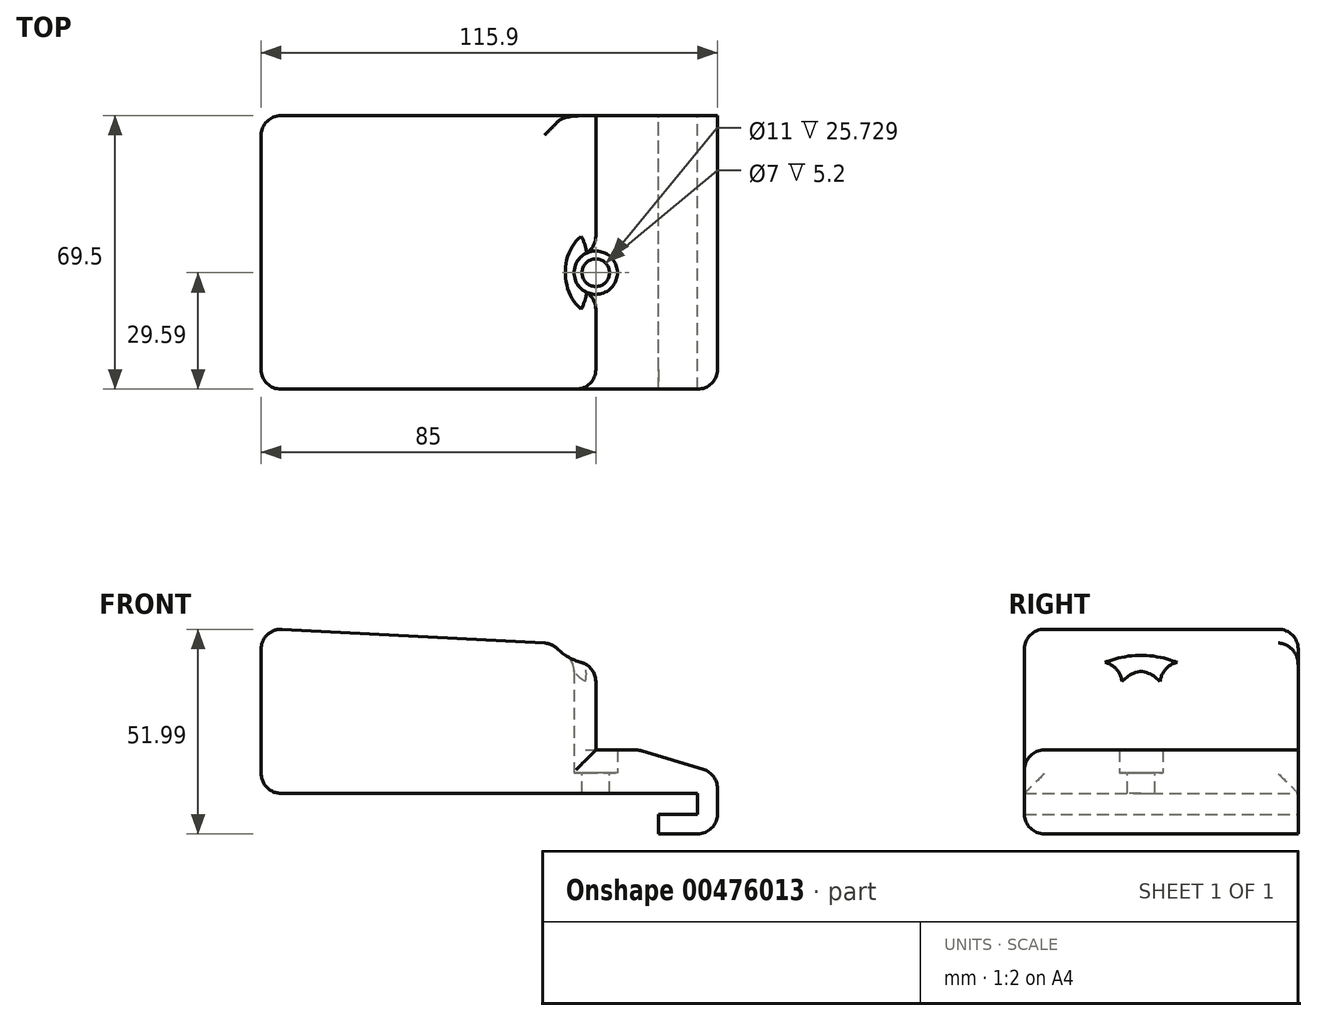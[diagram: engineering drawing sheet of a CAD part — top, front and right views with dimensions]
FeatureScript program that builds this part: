
annotation { "Feature Type Name" : "Feature", "Feature Type Description" : "" }
export const myFeature = defineFeature(function(context is Context, id is Id, definition is map)
    precondition{}
    {
        {
            var Q0;
            Q0=qCreatedBy(makeId("Front.planeOp"),FACE);
            var sketch = newSketch(context, id + "F0", { "sketchPlane" : qUnion([Q0])});
            skLineSegment(sketch, "E0", {"start": v(0, 37.5) * mm, "end": v(-85, 41.95) * mm});
            skLineSegment(sketch, "E1", {"start": v(-85, 41.95) * mm, "end": v(-85, 0) * mm});
            skLineSegment(sketch, "E2", {"start": v(0, 37.5) * mm, "end": v(0, 11) * mm});
            skLineSegment(sketch, "E3", {"start": v(0, 11) * mm, "end": v(11, 11) * mm});
            skLineSegment(sketch, "E4", {"start": v(30.9, 0) * mm, "end": v(30.9, -10.3) * mm});
            skLineSegment(sketch, "E5", {"start": v(30.9, -10.3) * mm, "end": v(15.9, -10.3) * mm});
            skLineSegment(sketch, "E6", {"start": v(15.9, -10.3) * mm, "end": v(15.9, -5.3) * mm});
            skLineSegment(sketch, "E7", {"start": v(15.9, -5.3) * mm, "end": v(25.9, -5.3) * mm});
            skLineSegment(sketch, "E8", {"start": v(25.9, -5.3) * mm, "end": v(25.9, 0) * mm});
            skLineSegment(sketch, "E9", {"start": v(25.9, 0) * mm, "end": v(-85, 0) * mm});
            skLineSegment(sketch, "E10", {"start": v(30.9, 0) * mm, "end": v(30.9, 5) * mm});
            skLineSegment(sketch, "E11", {"start": v(11, 11) * mm, "end": v(30.9, 5) * mm});
            skSolve(sketch);
        }
        {
            var Q0;
            Q0 = qSketchRegion(id + "F0", true);
            extrude(context, id + "F1", {"entities" : qUnion([Q0]), "depth" : 69.5 * mm});
        }
        {
            var Q0;
            Q0=makeQuery(id+"F1.opExtrude","CAP_FACE",FACE,{"disambiguationData":[OSD([sQuery(id+"F0.wireOp",EDGE,"E0"),sQuery(id+"F0.wireOp",EDGE,"E1"),sQuery(id+"F0.wireOp",EDGE,"Xl3YUMXG-rWPs-34HO-qeN5-JV3TIRV4gZtY"),sQuery(id+"F0.wireOp",EDGE,"MgZQELxX-fbr9-p0Fq-y226-Uqsu6zS7fgz1")])],"isStart":true});
            var sketch = newSketch(context, id + "F2", { "sketchPlane" : qUnion([Q0])});
            skCircle(sketch, "E12", {"center": v(0, 46.76) * mm, "radius": 14 * mm});
            skSolve(sketch);
        }
        {
            var Q0;
            Q0 = qSketchRegion(id + "F2", true);
            extrude(context, id + "F3", {"entities" : qUnion([Q0]), "operationType" : NewBodyOperationType.REMOVE, "endBound" : BoundingType.THROUGH_ALL, "oppositeDirection" : true, "depth" : 25 * mm});
        }
        {
            var Q0;
            Q0=makeQuery(id+"F1.opExtrude","SWEPT_FACE",FACE,{"disambiguationData":[OSD([sQuery(id+"F0.wireOp",EDGE,"E3")])]});
            var sketch = newSketch(context, id + "F4", { "sketchPlane" : qUnion([Q0])});
            skCircle(sketch, "E13", {"center": v(0, -39.91) * mm, "radius": 5.5 * mm});
            skSolve(sketch);
        }
        {
            var Q0;
            Q0 = qSketchRegion(id + "F4", true);
            extrude(context, id + "F5", {"entities" : qUnion([Q0]), "operationType" : NewBodyOperationType.REMOVE, "endBound" : BoundingType.THROUGH_ALL, "depth" : 25 * mm});
        }
        {
            var Q0;
            Q0 = qSketchRegion(id + "F4", true);
            extrude(context, id + "F6", {"entities" : qUnion([Q0]), "operationType" : NewBodyOperationType.REMOVE, "oppositeDirection" : true, "depth" : 5.8 * mm});
        }
        {
            var Q0;
            Q0=makeQuery(id+"F5.boolean.opBoolean","MERGE",FACE,{"derivedFrom":[makeQuery(id+"F1.opExtrude","SWEPT_FACE",FACE,{"disambiguationData":[OSD([sQuery(id+"F0.wireOp",EDGE,"E3")])]}),makeQuery(id+"F5.opExtrude","CAP_FACE",FACE,{"disambiguationData":[OSD([sQuery(id+"F4.wireOp",EDGE,"E13")])],"isStart":true})]});
            var sketch = newSketch(context, id + "F7", { "sketchPlane" : qUnion([Q0])});
            skCircle(sketch, "E14", {"center": v(0, -39.91) * mm, "radius": 3.5 * mm});
            skSolve(sketch);
        }
        {
            var Q0;
            Q0 = qSketchRegion(id + "F7", true);
            extrude(context, id + "F8", {"entities" : qUnion([Q0]), "operationType" : NewBodyOperationType.REMOVE, "endBound" : BoundingType.THROUGH_ALL, "oppositeDirection" : true, "depth" : 25 * mm});
        }
        {
            var Q0;
            Q0=makeQuery(id+"F1.opExtrude","SWEPT_EDGE",EDGE,{"disambiguationData":[OSD([sQuery(id+"F0.wireOp",EDGE,"E10"),sQuery(id+"F0.wireOp",EDGE,"E11")])]});
            var Q1;
            Q1=makeQuery(id+"F1.opExtrude","SWEPT_EDGE",EDGE,{"disambiguationData":[OSD([sQuery(id+"F0.wireOp",EDGE,"E3"),sQuery(id+"F0.wireOp",EDGE,"E11")])]});
            var Q2;
            Q2=makeQuery(id+"F1.opExtrude","CAP_EDGE",EDGE,{"disambiguationData":[OSD([sQuery(id+"F0.wireOp",EDGE,"E11")])],"isStart":false});
            var Q3;
            Q3=makeQuery(id+"F1.opExtrude","CAP_EDGE",EDGE,{"disambiguationData":[OSD([sQuery(id+"F0.wireOp",EDGE,"E3")])],"isStart":false});
            var Q4;
            Q4=makeQuery(id+"F1.opExtrude","CAP_EDGE",EDGE,{"disambiguationData":[OSD([sQuery(id+"F0.wireOp",EDGE,"E4"),sQuery(id+"F0.wireOp",EDGE,"E10")])],"isStart":false});
            var Q5;
            Q5=makeQuery(id+"F1.opExtrude","SWEPT_EDGE",EDGE,{"disambiguationData":[OSD([sQuery(id+"F0.wireOp",EDGE,"E4"),sQuery(id+"F0.wireOp",EDGE,"E5")])]});
            var Q6;
            Q6=makeQuery(id+"F1.opExtrude","CAP_EDGE",EDGE,{"disambiguationData":[OSD([sQuery(id+"F0.wireOp",EDGE,"E5")])],"isStart":false});
            var Q7;
            {var subQ0=sQuery(id+"F0.wireOp",EDGE,"E2");var subQ1=makeQuery(id+"F1.opExtrude","SWEPT_FACE",FACE,{"disambiguationData":[OSD([subQ0])]});var subQ2=makeQuery(id+"F3.opExtrude","SWEPT_FACE",FACE,{"disambiguationData":[OSD([sQuery(id+"F2.wireOp",EDGE,"E12")])]});Q7=makeQuery(id+"F5.boolean.opBoolean","SPLIT",EDGE,{"disambiguationData":[TD([makeQuery(id+"F1.opExtrude","CAP_FACE",FACE,{"disambiguationData":[OSD([sQuery(id+"F0.wireOp",EDGE,"E0"),sQuery(id+"F0.wireOp",EDGE,"E1"),subQ0,sQuery(id+"F0.wireOp",EDGE,"E3"),sQuery(id+"F0.wireOp",EDGE,"E4"),sQuery(id+"F0.wireOp",EDGE,"E5"),sQuery(id+"F0.wireOp",EDGE,"E6"),sQuery(id+"F0.wireOp",EDGE,"E7"),sQuery(id+"F0.wireOp",EDGE,"E8"),sQuery(id+"F0.wireOp",EDGE,"E9"),sQuery(id+"F0.wireOp",EDGE,"E10"),sQuery(id+"F0.wireOp",EDGE,"E11")])],"isStart":false})])],"derivedFrom":makeQuery(id+"F3.boolean.opBoolean","INTERSECT",EDGE,{"derivedFrom":[subQ1,subQ2]})});}
            var Q8;
            {var subQ0=sQuery(id+"F0.wireOp",EDGE,"E2");var subQ1=makeQuery(id+"F1.opExtrude","SWEPT_FACE",FACE,{"disambiguationData":[OSD([subQ0])]});var subQ2=makeQuery(id+"F3.opExtrude","SWEPT_FACE",FACE,{"disambiguationData":[OSD([sQuery(id+"F2.wireOp",EDGE,"E12")])]});Q8=makeQuery(id+"F5.boolean.opBoolean","SPLIT",EDGE,{"disambiguationData":[TD([makeQuery(id+"F1.opExtrude","CAP_FACE",FACE,{"disambiguationData":[OSD([sQuery(id+"F0.wireOp",EDGE,"E0"),sQuery(id+"F0.wireOp",EDGE,"E1"),subQ0,sQuery(id+"F0.wireOp",EDGE,"E3"),sQuery(id+"F0.wireOp",EDGE,"E4"),sQuery(id+"F0.wireOp",EDGE,"E5"),sQuery(id+"F0.wireOp",EDGE,"E6"),sQuery(id+"F0.wireOp",EDGE,"E7"),sQuery(id+"F0.wireOp",EDGE,"E8"),sQuery(id+"F0.wireOp",EDGE,"E9"),sQuery(id+"F0.wireOp",EDGE,"E10"),sQuery(id+"F0.wireOp",EDGE,"E11")])],"isStart":true})])],"derivedFrom":makeQuery(id+"F3.boolean.opBoolean","INTERSECT",EDGE,{"derivedFrom":[subQ1,subQ2]})});}
            var Q9;
            Q9=makeQuery(id+"F3.boolean.opBoolean","INTERSECT",EDGE,{"derivedFrom":[makeQuery(id+"F1.opExtrude","SWEPT_FACE",FACE,{"disambiguationData":[OSD([sQuery(id+"F0.wireOp",EDGE,"E0")])]}),makeQuery(id+"F3.opExtrude","SWEPT_FACE",FACE,{"disambiguationData":[OSD([sQuery(id+"F2.wireOp",EDGE,"E12")])]})]});
            var Q10;
            Q10=makeQuery(id+"F1.opExtrude","CAP_EDGE",EDGE,{"disambiguationData":[OSD([sQuery(id+"F0.wireOp",EDGE,"E2")])],"isStart":false});
            var Q11;
            Q11=makeQuery(id+"F5.boolean.opBoolean","INTERSECT",EDGE,{"disambiguationData":[OD(0.0)],"derivedFrom":[makeQuery(id+"F1.opExtrude","SWEPT_FACE",FACE,{"disambiguationData":[OSD([sQuery(id+"F0.wireOp",EDGE,"E2")])]}),makeQuery(id+"F5.opExtrude","SWEPT_FACE",FACE,{"disambiguationData":[OSD([sQuery(id+"F4.wireOp",EDGE,"E13")])]})]});
            var Q12;
            Q12=makeQuery(id+"F5.boolean.opBoolean","INTERSECT",EDGE,{"disambiguationData":[OD(1.0)],"derivedFrom":[makeQuery(id+"F1.opExtrude","SWEPT_FACE",FACE,{"disambiguationData":[OSD([sQuery(id+"F0.wireOp",EDGE,"E2")])]}),makeQuery(id+"F5.opExtrude","SWEPT_FACE",FACE,{"disambiguationData":[OSD([sQuery(id+"F4.wireOp",EDGE,"E13")])]})]});
            var Q13;
            Q13=makeQuery(id+"F5.boolean.opBoolean","INTERSECT",EDGE,{"derivedFrom":[makeQuery(id+"F3.boolean.opBoolean","COPY",FACE,{"derivedFrom":makeQuery(id+"F3.opExtrude","SWEPT_FACE",FACE,{"disambiguationData":[OSD([sQuery(id+"F2.wireOp",EDGE,"E12")])]})}),makeQuery(id+"F5.opExtrude","SWEPT_FACE",FACE,{"disambiguationData":[OSD([sQuery(id+"F4.wireOp",EDGE,"E13")])]})]});
            var Q14;
            Q14=makeQuery(id+"F3.boolean.opBoolean","INTERSECT",EDGE,{"derivedFrom":[makeQuery(id+"F1.opExtrude","CAP_FACE",FACE,{"disambiguationData":[OSD([sQuery(id+"F0.wireOp",EDGE,"E0"),sQuery(id+"F0.wireOp",EDGE,"E1"),sQuery(id+"F0.wireOp",EDGE,"E2"),sQuery(id+"F0.wireOp",EDGE,"E3"),sQuery(id+"F0.wireOp",EDGE,"E4"),sQuery(id+"F0.wireOp",EDGE,"E5"),sQuery(id+"F0.wireOp",EDGE,"E6"),sQuery(id+"F0.wireOp",EDGE,"E7"),sQuery(id+"F0.wireOp",EDGE,"E8"),sQuery(id+"F0.wireOp",EDGE,"E9"),sQuery(id+"F0.wireOp",EDGE,"E10"),sQuery(id+"F0.wireOp",EDGE,"E11")])],"isStart":false}),makeQuery(id+"F3.opExtrude","SWEPT_FACE",FACE,{"disambiguationData":[OSD([sQuery(id+"F2.wireOp",EDGE,"E12")])]})]});
            var Q15;
            Q15=makeQuery(id+"F1.opExtrude","CAP_EDGE",EDGE,{"disambiguationData":[OSD([sQuery(id+"F0.wireOp",EDGE,"E0")])],"isStart":false});
            var Q16;
            Q16=makeQuery(id+"F1.opExtrude","CAP_EDGE",EDGE,{"disambiguationData":[OSD([sQuery(id+"F0.wireOp",EDGE,"E1")])],"isStart":false});
            var Q17;
            Q17=makeQuery(id+"F1.opExtrude","SWEPT_EDGE",EDGE,{"disambiguationData":[OSD([sQuery(id+"F0.wireOp",EDGE,"E0"),sQuery(id+"F0.wireOp",EDGE,"E1")])]});
            var Q18;
            Q18=makeQuery(id+"F1.opExtrude","CAP_EDGE",EDGE,{"disambiguationData":[OSD([sQuery(id+"F0.wireOp",EDGE,"E0")])],"isStart":true});
            var Q19;
            Q19=makeQuery(id+"F1.opExtrude","SWEPT_FACE",FACE,{"disambiguationData":[OSD([sQuery(id+"F0.wireOp",EDGE,"E1")])]});
            fillet(context, id + "F9", {"entities" : qUnion([Q0, Q1, Q2, Q3, Q4, Q5, Q6, Q7, Q8, Q9, Q10, Q11, Q12, Q13, Q14, Q15, Q16, Q17, Q18, Q19]), "radius" : 5 * mm, "tangentPropagation" : true, "allowEdgeOverflow" : false});
        }
    });
